# Revit family: Resideo_Thermostat_T4H310A3032a
name_source: partatom
category: Electrical Fixtures
units: mm (PartAtom-declared; Revit-internal decimal feet)

## family parameters
Cut with Voids When Loaded = No
Host = Face
Maintain Annotation Orientation = No
OmniClass Number = 23.75.65.11.11
OmniClass Title = Heating Controllers
Part Type = Normal
Room Calculation Point = No
Round Connector Dimension = Use Diameter
Shared = No

## types (1)
- T4H310A3032
    Assembly Code = D3060
    AssetType = Fixed
    BIMObjectName = Resideo_Thermostat_T4H310A3032
    ClassificationName = Uniclass2015
    ClassificationValue = Pr_75_50_76_73
    Cost = 0 $
    Default Elevation = 0 mm  [stored 0 ft]
    Description = T4M WIRED OT THERMOSTAT
    DisplayMaterial = Resideo - Screen - Green
    DocumentationCertificates = https://www.bimstore.co
    DocumentationInstallationGuide = https://www.bimstore.co
    DocumentationLiterature = https://www.bimstore.co
    DocumentationMaintenance = https://www.bimstore.co
    DocumentationTechnical = https://www.bimstore.co
    DurationUnit = Years
    ExpectedLife = 0
    IfcExportAs = IfcUnitaryControlElement
    IfcExportType = IfcUnitaryControlElementTypeEnum.CONTROLPANEL
    Keynote = W
    Manufacturer = Resideo
    ManufacturerName = Resideo
    Model = T4H310A3032
    ModelNumber = T4H310A3032
    ModelReference = T4M WIRED OT THERMOSTAT
    NBSDescription = Room temperature sensors
    NBSObjectName = Resideo - Room temperature sensors
    NominalDepth = 28 mm  [stored 0.0918635 ft]
    NominalHeight = 97 mm  [stored 0.318241 ft]
    NominalLength = 136 mm
    PrimaryMaterial = Resideo - Plastic - White
    ProductionYear = 2022
    SecondaryMaterial = Resideo - Plastic - Dark Grey
    Size = 28mm (D) x 97mm (H) x 136mm (L)
    Type Comments = T4M WIRED OT THERMOSTAT
    TypeName = T4H310A3032 - T4M WIRED OT THERMOSTAT
    URL = https://www.resideo.com
    WarrantyDurationLabor = 0
    WarrantyDurationParts = 0
    WarrantyDurationUnit = Years
    WarrantyGuarantorLabor = https://www.resideo.com
    WarrantyGuarantorParts = https://www.resideo.com
    _BSBibleVersion = 16
    _BimSpecGuid = 0
    _CurrentRevision = 1
    _DistributedBy = https://www.bimstore.co
    _ObjectUserGuide = https://www.bimstore.co

note: [stored X ft] marks values corroborated as IEEE doubles in the binary element streams (Revit-internal decimal feet)

## geometry (parser evidence)
native form markers: Sweep x1
no freeform markers — native parametric forms only
